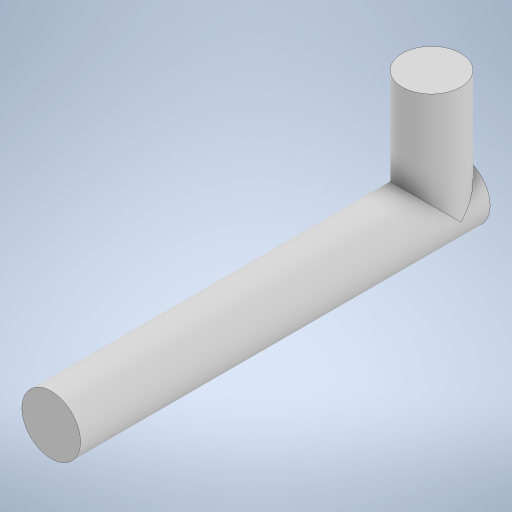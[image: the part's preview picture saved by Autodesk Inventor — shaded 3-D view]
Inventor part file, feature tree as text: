
AUTODESK INVENTOR PART (.ipt)
format: ipt  version: 2023 (Build 270158000, 158)  size: 541,184 bytes
history: native  units: in
note: dims shown in document units (in); Inventor stores cm internally (conversion verified against a paired STEP export)
features: extrude x2, sketch x2
ambient origin geometry x8: Origin, YZ Plane, XZ Plane, XY Plane, X Axis, Y Axis, Z Axis, Center Point
bodies: Solid1 (feature_tree)
feature tree (4):
  extrude  "Extrusion1"  Depth=1.6535in TaperAngle=0.0deg
  extrude  "Extrusion2"  Depth=0.1181in
  sketch  "Sketch1"  dims[d0=0.2362in d1=1.6535in d2=0.0in]
  sketch  "Sketch2"  dims[d3=0.1181in d4=0.2362in d5=0.4724in d6=0.0in]
